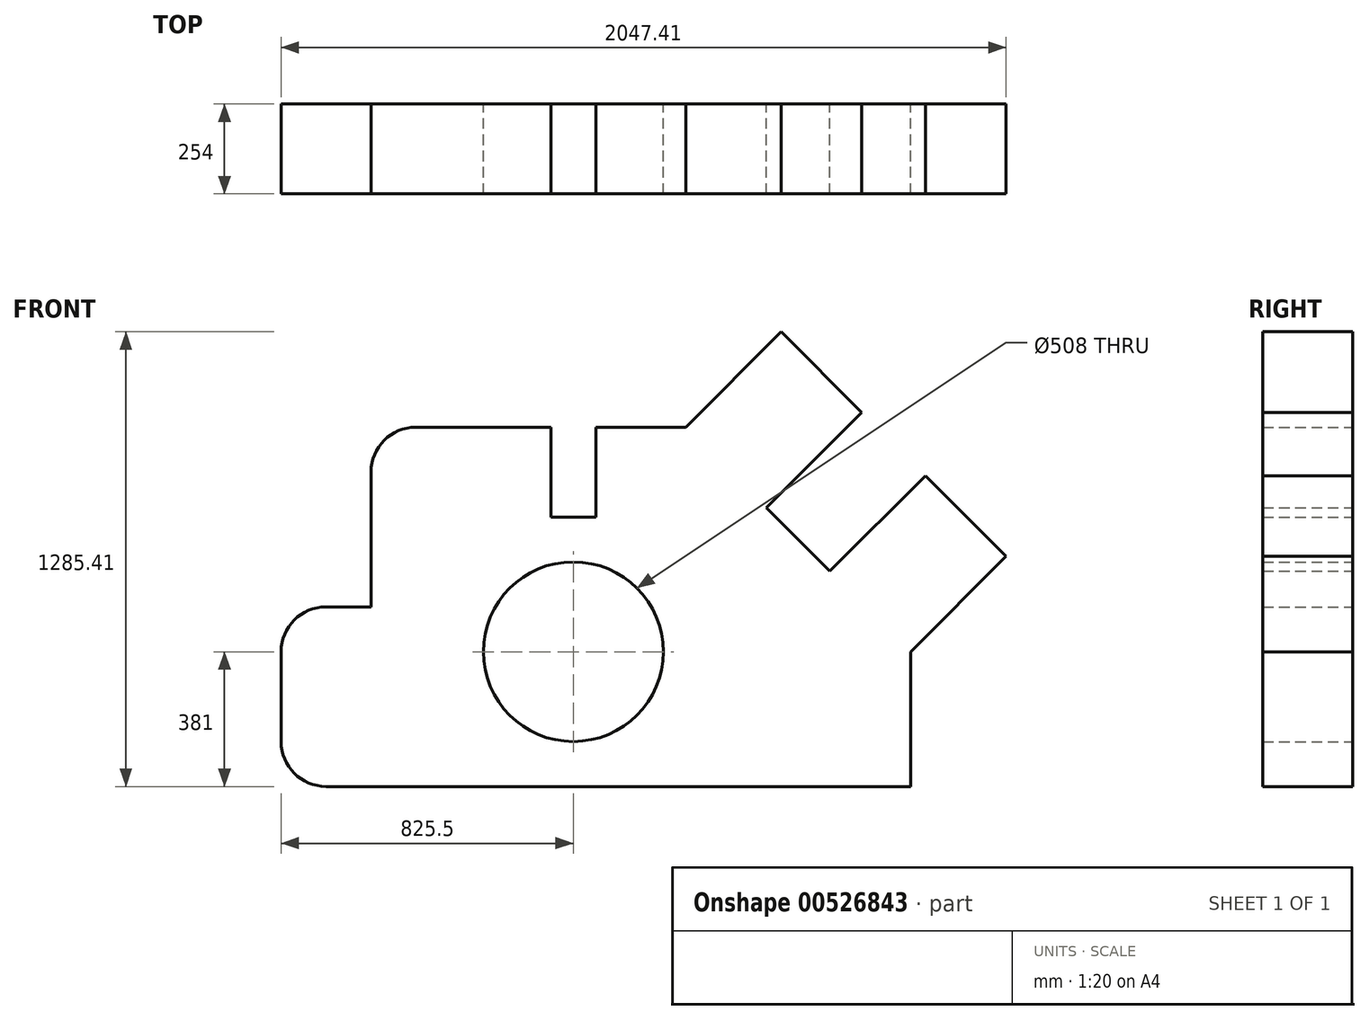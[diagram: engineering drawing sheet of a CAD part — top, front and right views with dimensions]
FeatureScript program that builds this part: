
annotation { "Feature Type Name" : "Feature", "Feature Type Description" : "" }
export const myFeature = defineFeature(function(context is Context, id is Id, definition is map)
    precondition{}
    {
        {
            var Q0;
            Q0=qCreatedBy(makeId("Front.planeOp"),FACE);
            var sketch = newSketch(context, id + "F0", { "sketchPlane" : qUnion([Q0])});
            skLineSegment(sketch, "E0", {"start": v(127, 0) * mm, "end": v(1778, 0) * mm});
            skLineSegment(sketch, "E1", {"start": v(0, 127) * mm, "end": v(0, 381) * mm});
            skPoint(sketch, "E2.visualSharp", {"position": v(0, 0) * mm});
            skArc(sketch, "E2.filletArc", {"start": v(0, 127) * mm, "mid": v(37.2, 37.2) * mm, "end": v(127, 0) * mm});
            skLineSegment(sketch, "E3", {"start": v(1778, 0) * mm, "end": v(1778, 381) * mm});
            skCircle(sketch, "E4", {"center": v(825.5, 381) * mm, "radius": 254 * mm});
            skLineSegment(sketch, "E5", {"start": v(127, 508) * mm, "end": v(254, 508) * mm});
            skPoint(sketch, "E6.visualSharp", {"position": v(0, 508) * mm});
            skArc(sketch, "E6.filletArc", {"start": v(127, 508) * mm, "mid": v(37.2, 470.8) * mm, "end": v(0, 381) * mm});
            skLineSegment(sketch, "E7", {"start": v(254, 508) * mm, "end": v(254, 889) * mm});
            skLineSegment(sketch, "E8", {"start": v(381, 1016) * mm, "end": v(762, 1016) * mm});
            skLineSegment(sketch, "E9", {"start": v(762, 1016) * mm, "end": v(762, 762) * mm});
            skLineSegment(sketch, "E10", {"start": v(762, 762) * mm, "end": v(889, 762) * mm});
            skLineSegment(sketch, "E11", {"start": v(889, 762) * mm, "end": v(889, 1016) * mm});
            skLineSegment(sketch, "E12", {"start": v(889, 1016) * mm, "end": v(1143, 1016) * mm});
            skPoint(sketch, "E13.visualSharp", {"position": v(254, 1016) * mm});
            skArc(sketch, "E13.filletArc", {"start": v(381, 1016) * mm, "mid": v(291.2, 978.8) * mm, "end": v(254, 889) * mm});
            skLineSegment(sketch, "E14", {"start": v(1778, 381) * mm, "end": v(2047.4, 650.4) * mm});
            skLineSegment(sketch, "E15", {"start": v(2047.4, 650.4) * mm, "end": v(1819.71, 878.1) * mm});
            skLineSegment(sketch, "E16", {"start": v(1819.71, 878.1) * mm, "end": v(1550.3, 608.7) * mm});
            skLineSegment(sketch, "E17", {"start": v(1550.3, 608.7) * mm, "end": v(1370.7, 788.3) * mm});
            skLineSegment(sketch, "E18", {"start": v(1370.7, 788.3) * mm, "end": v(1640.1, 1057.71) * mm});
            skLineSegment(sketch, "E19", {"start": v(1640.1, 1057.71) * mm, "end": v(1412.4, 1285.4) * mm});
            skLineSegment(sketch, "E20", {"start": v(1412.4, 1285.4) * mm, "end": v(1143, 1016) * mm});
            skSolve(sketch);
        }
        {
            var Q0;
            Q0=makeQuery(id+"F0.imprint","IMPRINT",FACE,{"disambiguationData":[TD([[makeQuery(id+"F0.imprint","IMPRINT",EDGE,{"derivedFrom":sQuery(id+"F0.wireOp",EDGE,"E0")}),1.0]])]});
            extrude(context, id + "F1", {"entities" : qUnion([Q0]), "depth" : 254 * mm, "offsetDistance" : 25.4 * mm});
        }
    });
